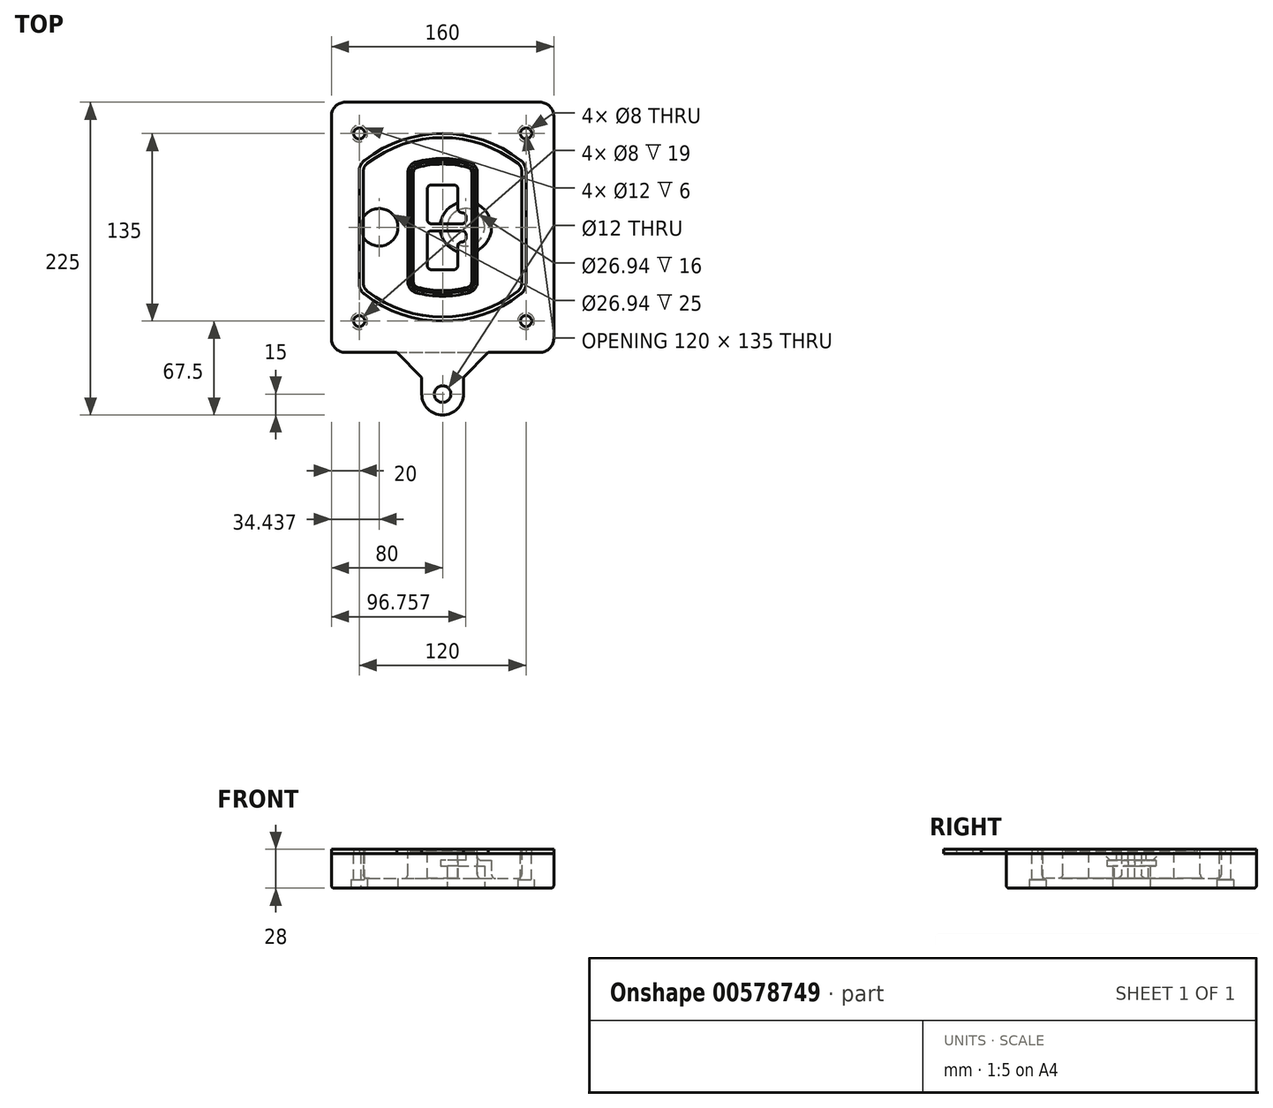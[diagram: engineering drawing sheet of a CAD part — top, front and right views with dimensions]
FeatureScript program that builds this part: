
annotation { "Feature Type Name" : "Feature", "Feature Type Description" : "" }
export const myFeature = defineFeature(function(context is Context, id is Id, definition is map)
    precondition{}
    {
        {
            var Q0;
            Q0=qCreatedBy(makeId("Top.planeOp"),FACE);
            var sketch = newSketch(context, id + "F0", { "sketchPlane" : qUnion([Q0])});
            skPoint(sketch, "E0.rect.middle", {"position": v(0, 0) * mm});
            skLineSegment(sketch, "E1.bottom", {"start": v(-70, -90) * mm, "end": v(70, -90) * mm});
            skLineSegment(sketch, "E1.top", {"start": v(-70, 90) * mm, "end": v(70, 90) * mm});
            skLineSegment(sketch, "E1.left", {"start": v(-80, -80) * mm, "end": v(-80, 80) * mm});
            skLineSegment(sketch, "E1.right", {"start": v(80, -80) * mm, "end": v(80, 80) * mm});
            skLineSegment(sketch, "E2", {"start": v(-80, 90) * mm, "end": v(80, -90) * mm, "construction": true});
            skLineSegment(sketch, "E3", {"start": v(80, 90) * mm, "end": v(-80, -90) * mm, "construction": true});
            skCircle(sketch, "E4", {"center": v(-60, 67.5) * mm, "radius": 4 * mm});
            skCircle(sketch, "E5", {"center": v(60, 67.5) * mm, "radius": 4 * mm});
            skCircle(sketch, "E6", {"center": v(60, -67.5) * mm, "radius": 4 * mm});
            skCircle(sketch, "E7", {"center": v(-60, -67.5) * mm, "radius": 4 * mm});
            skLineSegment(sketch, "E8", {"start": v(-60, 67.5) * mm, "end": v(60, 67.5) * mm, "construction": true});
            skLineSegment(sketch, "E9", {"start": v(60, 67.5) * mm, "end": v(60, -67.5) * mm, "construction": true});
            skLineSegment(sketch, "E10", {"start": v(60, -67.5) * mm, "end": v(-60, -67.5) * mm, "construction": true});
            skLineSegment(sketch, "E11", {"start": v(-60, -67.5) * mm, "end": v(-60, 67.5) * mm, "construction": true});
            skLineSegment(sketch, "E12", {"start": v(-60, 40.3) * mm, "end": v(-60, -40.3) * mm});
            skLineSegment(sketch, "E13", {"start": v(60, 40.3) * mm, "end": v(60, -40.3) * mm});
            skArc(sketch, "E14", {"start": v(56.15, 48.18) * mm, "mid": v(0, 67.5) * mm, "end": v(-56.15, 48.18) * mm});
            skArc(sketch, "E15", {"start": v(-56.15, -48.18) * mm, "mid": v(0, -67.5) * mm, "end": v(56.15, -48.18) * mm});
            skLineSegment(sketch, "E16", {"start": v(-60, 0) * mm, "end": v(60, 0) * mm, "construction": true});
            skPoint(sketch, "E17.visualSharp", {"position": v(-60, -45) * mm});
            skArc(sketch, "E17.filletArc", {"start": v(-60, -40.3) * mm, "mid": v(-58.99, -44.68) * mm, "end": v(-56.15, -48.18) * mm});
            skPoint(sketch, "E18.visualSharp", {"position": v(-60, 45) * mm});
            skArc(sketch, "E18.filletArc", {"start": v(-56.15, 48.18) * mm, "mid": v(-58.99, 44.68) * mm, "end": v(-60, 40.3) * mm});
            skPoint(sketch, "E19.visualSharp", {"position": v(60, 45) * mm});
            skArc(sketch, "E19.filletArc", {"start": v(60, 40.3) * mm, "mid": v(58.99, 44.68) * mm, "end": v(56.15, 48.18) * mm});
            skPoint(sketch, "E20.visualSharp", {"position": v(60, -45) * mm});
            skArc(sketch, "E20.filletArc", {"start": v(56.15, -48.18) * mm, "mid": v(58.99, -44.68) * mm, "end": v(60, -40.3) * mm});
            skPoint(sketch, "E21.visualSharp", {"position": v(-80, 90) * mm});
            skArc(sketch, "E21.filletArc", {"start": v(-70, 90) * mm, "mid": v(-77.07, 87.07) * mm, "end": v(-80, 80) * mm});
            skPoint(sketch, "E22.visualSharp", {"position": v(80, 90) * mm});
            skArc(sketch, "E22.filletArc", {"start": v(80, 80) * mm, "mid": v(77.07, 87.07) * mm, "end": v(70, 90) * mm});
            skPoint(sketch, "E23.visualSharp", {"position": v(80, -90) * mm});
            skArc(sketch, "E23.filletArc", {"start": v(70, -90) * mm, "mid": v(77.07, -87.07) * mm, "end": v(80, -80) * mm});
            skPoint(sketch, "E24.visualSharp", {"position": v(-80, -90) * mm});
            skArc(sketch, "E24.filletArc", {"start": v(-80, -80) * mm, "mid": v(-77.07, -87.07) * mm, "end": v(-70, -90) * mm});
            skArc(sketch, "E25.0", {"start": v(57, 40.3) * mm, "mid": v(56.3, 43.36) * mm, "end": v(54.3, 45.81) * mm});
            skLineSegment(sketch, "E25.1", {"start": v(57, 40.3) * mm, "end": v(57, -40.3) * mm});
            skArc(sketch, "E25.2", {"start": v(54.3, -45.81) * mm, "mid": v(56.3, -43.36) * mm, "end": v(57, -40.3) * mm});
            skArc(sketch, "E25.3", {"start": v(-54.3, -45.81) * mm, "mid": v(0, -64.5) * mm, "end": v(54.3, -45.81) * mm});
            skArc(sketch, "E25.4", {"start": v(-57, -40.3) * mm, "mid": v(-56.3, -43.36) * mm, "end": v(-54.3, -45.81) * mm});
            skArc(sketch, "E25.5", {"start": v(54.3, 45.81) * mm, "mid": v(0, 64.5) * mm, "end": v(-54.3, 45.81) * mm});
            skLineSegment(sketch, "E25.6", {"start": v(-57, 40.3) * mm, "end": v(-57, -40.3) * mm});
            skArc(sketch, "E25.7", {"start": v(-54.3, 45.81) * mm, "mid": v(-56.3, 43.36) * mm, "end": v(-57, 40.3) * mm});
            skArc(sketch, "E26.0", {"start": v(-58.62, 51.33) * mm, "mid": v(-62.58, 46.43) * mm, "end": v(-64, 40.3) * mm});
            skArc(sketch, "E26.1", {"start": v(58.62, 51.33) * mm, "mid": v(0, 71.5) * mm, "end": v(-58.62, 51.33) * mm});
            skArc(sketch, "E26.2", {"start": v(64, 40.3) * mm, "mid": v(62.58, 46.43) * mm, "end": v(58.62, 51.33) * mm});
            skLineSegment(sketch, "E26.3", {"start": v(64, 40.3) * mm, "end": v(64, -40.3) * mm});
            skArc(sketch, "E26.4", {"start": v(58.62, -51.33) * mm, "mid": v(62.58, -46.43) * mm, "end": v(64, -40.3) * mm});
            skLineSegment(sketch, "E26.5", {"start": v(-64, 40.3) * mm, "end": v(-64, -40.3) * mm});
            skArc(sketch, "E26.6", {"start": v(-58.62, -51.33) * mm, "mid": v(0, -71.5) * mm, "end": v(58.62, -51.33) * mm});
            skArc(sketch, "E26.7", {"start": v(-64, -40.3) * mm, "mid": v(-62.58, -46.43) * mm, "end": v(-58.62, -51.33) * mm});
            skSolve(sketch);
        }
        {
            var Q0;
            Q0=makeQuery(id+"F0.imprint","IMPRINT",FACE,{"disambiguationData":[TD([[makeQuery(id+"F0.imprint","IMPRINT",EDGE,{"derivedFrom":sQuery(id+"F0.wireOp",EDGE,"E1.bottom")}),1.0]])]});
            var Q1;
            Q1=makeQuery(id+"F0.imprint","IMPRINT",FACE,{"disambiguationData":[TD([[makeQuery(id+"F0.imprint","IMPRINT",EDGE,{"derivedFrom":sQuery(id+"F0.wireOp",EDGE,"E12")}),1.0]])]});
            var Q2;
            Q2=makeQuery(id+"F0.imprint","IMPRINT",FACE,{"disambiguationData":[TD([[makeQuery(id+"F0.imprint","IMPRINT",EDGE,{"derivedFrom":sQuery(id+"F0.wireOp",EDGE,"E25.0")}),1.0]])]});
            var Q3;
            Q3=makeQuery(id+"F0.imprint","IMPRINT",FACE,{"disambiguationData":[TD([[makeQuery(id+"F0.imprint","IMPRINT",EDGE,{"derivedFrom":sQuery(id+"F0.wireOp",EDGE,"E12")}),-1.0]])]});
            extrude(context, id + "F1", {"entities" : qUnion([Q0, Q1, Q2, Q3]), "oppositeDirection" : true, "depth" : 25 * mm});
        }
        {
            var Q0;
            Q0=makeQuery(id+"F0.imprint","IMPRINT",FACE,{"disambiguationData":[TD([[makeQuery(id+"F0.imprint","IMPRINT",EDGE,{"derivedFrom":sQuery(id+"F0.wireOp",EDGE,"E12")}),1.0]])]});
            extrude(context, id + "F2", {"entities" : qUnion([Q0]), "operationType" : NewBodyOperationType.ADD, "depth" : 3 * mm});
        }
        {
            var Q0;
            Q0=makeQuery(id+"F0.imprint","IMPRINT",FACE,{"disambiguationData":[TD([[makeQuery(id+"F0.imprint","IMPRINT",EDGE,{"derivedFrom":sQuery(id+"F0.wireOp",EDGE,"E25.0")}),1.0]])]});
            extrude(context, id + "F3", {"entities" : qUnion([Q0]), "operationType" : NewBodyOperationType.REMOVE, "oppositeDirection" : true, "depth" : 18 * mm});
        }
        {
            var Q0;
            Q0=makeQuery(id+"F2.opExtrude","CAP_FACE",FACE,{"disambiguationData":[OSD([sQuery(id+"F0.wireOp",EDGE,"E12"),sQuery(id+"F0.wireOp",EDGE,"E13"),sQuery(id+"F0.wireOp",EDGE,"E14"),sQuery(id+"F0.wireOp",EDGE,"E15"),sQuery(id+"F0.wireOp",EDGE,"E17.filletArc"),sQuery(id+"F0.wireOp",EDGE,"E18.filletArc"),sQuery(id+"F0.wireOp",EDGE,"E19.filletArc"),sQuery(id+"F0.wireOp",EDGE,"E20.filletArc"),sQuery(id+"F0.wireOp",EDGE,"E25.0"),sQuery(id+"F0.wireOp",EDGE,"E25.1"),sQuery(id+"F0.wireOp",EDGE,"E25.2"),sQuery(id+"F0.wireOp",EDGE,"E25.3"),sQuery(id+"F0.wireOp",EDGE,"E25.4"),sQuery(id+"F0.wireOp",EDGE,"E25.5"),sQuery(id+"F0.wireOp",EDGE,"E25.6"),sQuery(id+"F0.wireOp",EDGE,"E25.7")])],"isStart":false});
            var sketch = newSketch(context, id + "F4", { "sketchPlane" : qUnion([Q0])});
            skArc(sketch, "E27.0", {"start": v(-19.08, -46.97) * mm, "mid": v(0, -49.5) * mm, "end": v(19.08, -46.97) * mm});
            skArc(sketch, "E28.0", {"start": v(19.08, 46.97) * mm, "mid": v(0, 49.5) * mm, "end": v(-19.08, 46.97) * mm});
            skLineSegment(sketch, "E29", {"start": v(-25, 39.25) * mm, "end": v(-25, -39.25) * mm});
            skLineSegment(sketch, "E30", {"start": v(25, 39.25) * mm, "end": v(25, -39.25) * mm});
            skLineSegment(sketch, "E31", {"start": v(-25, 45.1) * mm, "end": v(25, 45.1) * mm, "construction": true});
            skLineSegment(sketch, "E32", {"start": v(-25, -45.1) * mm, "end": v(25, -45.1) * mm, "construction": true});
            skPoint(sketch, "E33.visualSharp", {"position": v(-25, 45.1) * mm});
            skArc(sketch, "E33.filletArc", {"start": v(-19.08, 46.97) * mm, "mid": v(-23.35, 44.11) * mm, "end": v(-25, 39.25) * mm});
            skPoint(sketch, "E34.visualSharp", {"position": v(25, 45.1) * mm});
            skArc(sketch, "E34.filletArc", {"start": v(25, 39.25) * mm, "mid": v(23.35, 44.11) * mm, "end": v(19.08, 46.97) * mm});
            skPoint(sketch, "E35.visualSharp", {"position": v(25, -45.1) * mm});
            skArc(sketch, "E35.filletArc", {"start": v(19.08, -46.97) * mm, "mid": v(23.35, -44.11) * mm, "end": v(25, -39.25) * mm});
            skPoint(sketch, "E36.visualSharp", {"position": v(-25, -45.1) * mm});
            skArc(sketch, "E36.filletArc", {"start": v(-25, -39.25) * mm, "mid": v(-23.35, -44.11) * mm, "end": v(-19.08, -46.97) * mm});
            skArc(sketch, "E37.0", {"start": v(54.3, 45.81) * mm, "mid": v(0, 64.5) * mm, "end": v(-54.3, 45.81) * mm});
            skArc(sketch, "E37.1", {"start": v(-54.3, 45.81) * mm, "mid": v(-56.3, 43.36) * mm, "end": v(-57, 40.3) * mm});
            skLineSegment(sketch, "E37.2", {"start": v(-57, 40.3) * mm, "end": v(-57, -40.3) * mm});
            skArc(sketch, "E37.3", {"start": v(-57, -40.3) * mm, "mid": v(-56.3, -43.36) * mm, "end": v(-54.3, -45.81) * mm});
            skArc(sketch, "E37.4", {"start": v(-54.3, -45.81) * mm, "mid": v(0, -64.5) * mm, "end": v(54.3, -45.81) * mm});
            skArc(sketch, "E37.5", {"start": v(54.3, -45.81) * mm, "mid": v(56.3, -43.36) * mm, "end": v(57, -40.3) * mm});
            skLineSegment(sketch, "E37.6", {"start": v(57, 40.3) * mm, "end": v(57, -40.3) * mm});
            skArc(sketch, "E37.7", {"start": v(57, 40.3) * mm, "mid": v(56.3, 43.36) * mm, "end": v(54.3, 45.81) * mm});
            skLineSegment(sketch, "E38.0", {"start": v(23, 39.25) * mm, "end": v(23, -39.25) * mm});
            skArc(sketch, "E38.1", {"start": v(18.56, -45.04) * mm, "mid": v(21.76, -42.9) * mm, "end": v(23, -39.25) * mm});
            skArc(sketch, "E38.2", {"start": v(-18.56, -45.04) * mm, "mid": v(0, -47.5) * mm, "end": v(18.56, -45.04) * mm});
            skArc(sketch, "E38.3", {"start": v(-23, -39.25) * mm, "mid": v(-21.76, -42.9) * mm, "end": v(-18.56, -45.04) * mm});
            skLineSegment(sketch, "E38.4", {"start": v(-23, 39.25) * mm, "end": v(-23, -39.25) * mm});
            skArc(sketch, "E38.5", {"start": v(23, 39.25) * mm, "mid": v(21.76, 42.9) * mm, "end": v(18.56, 45.04) * mm});
            skArc(sketch, "E38.6", {"start": v(-18.56, 45.04) * mm, "mid": v(-21.76, 42.9) * mm, "end": v(-23, 39.25) * mm});
            skArc(sketch, "E38.7", {"start": v(18.56, 45.04) * mm, "mid": v(0, 47.5) * mm, "end": v(-18.56, 45.04) * mm});
            skArc(sketch, "E39.0", {"start": v(21, 39.25) * mm, "mid": v(20.18, 41.68) * mm, "end": v(18.04, 43.1) * mm});
            skLineSegment(sketch, "E39.1", {"start": v(21, 39.25) * mm, "end": v(21, -39.25) * mm});
            skArc(sketch, "E39.2", {"start": v(18.04, -43.1) * mm, "mid": v(20.18, -41.68) * mm, "end": v(21, -39.25) * mm});
            skArc(sketch, "E39.3", {"start": v(-18.04, -43.1) * mm, "mid": v(0, -45.5) * mm, "end": v(18.04, -43.1) * mm});
            skArc(sketch, "E39.4", {"start": v(-21, -39.25) * mm, "mid": v(-20.18, -41.68) * mm, "end": v(-18.04, -43.1) * mm});
            skArc(sketch, "E39.5", {"start": v(18.04, 43.1) * mm, "mid": v(0, 45.5) * mm, "end": v(-18.04, 43.1) * mm});
            skLineSegment(sketch, "E39.6", {"start": v(-21, 39.25) * mm, "end": v(-21, -39.25) * mm});
            skArc(sketch, "E39.7", {"start": v(-18.04, 43.1) * mm, "mid": v(-20.18, 41.68) * mm, "end": v(-21, 39.25) * mm});
            skLineSegment(sketch, "E40", {"start": v(-25, 0) * mm, "end": v(25, 0) * mm, "construction": true});
            skLineSegment(sketch, "E41", {"start": v(-11, 5.5) * mm, "end": v(-11, 27.5) * mm});
            skLineSegment(sketch, "E42", {"start": v(-8, 30.5) * mm, "end": v(8, 30.5) * mm});
            skLineSegment(sketch, "E43", {"start": v(11, 27.5) * mm, "end": v(11, 13.5) * mm});
            skLineSegment(sketch, "E44", {"start": v(14, 10.5) * mm, "end": v(14, 10.5) * mm});
            skLineSegment(sketch, "E45", {"start": v(17, 7.5) * mm, "end": v(17, 5.5) * mm});
            skLineSegment(sketch, "E46", {"start": v(14, 2.5) * mm, "end": v(-8, 2.5) * mm});
            skPoint(sketch, "E47.visualSharp", {"position": v(-11, 30.5) * mm});
            skArc(sketch, "E47.filletArc", {"start": v(-8, 30.5) * mm, "mid": v(-10.12, 29.62) * mm, "end": v(-11, 27.5) * mm});
            skPoint(sketch, "E48.visualSharp", {"position": v(11, 30.5) * mm});
            skArc(sketch, "E48.filletArc", {"start": v(11, 27.5) * mm, "mid": v(10.12, 29.62) * mm, "end": v(8, 30.5) * mm});
            skPoint(sketch, "E49.visualSharp", {"position": v(11, 10.5) * mm});
            skArc(sketch, "E49.filletArc", {"start": v(11, 13.5) * mm, "mid": v(11.88, 11.38) * mm, "end": v(14, 10.5) * mm});
            skPoint(sketch, "E50.visualSharp", {"position": v(17, 10.5) * mm});
            skArc(sketch, "E50.filletArc", {"start": v(17, 7.5) * mm, "mid": v(16.12, 9.62) * mm, "end": v(14, 10.5) * mm});
            skPoint(sketch, "E51.visualSharp", {"position": v(17, 2.5) * mm});
            skArc(sketch, "E51.filletArc", {"start": v(14, 2.5) * mm, "mid": v(16.12, 3.38) * mm, "end": v(17, 5.5) * mm});
            skPoint(sketch, "E52.visualSharp", {"position": v(-11, 2.5) * mm});
            skArc(sketch, "E52.filletArc", {"start": v(-11, 5.5) * mm, "mid": v(-10.12, 3.38) * mm, "end": v(-8, 2.5) * mm});
            skLineSegment(sketch, "E53.0.MirrorCS", {"start": v(14, -2.5) * mm, "end": v(-8, -2.5) * mm});
            skArc(sketch, "E54.0.MirrorCS", {"start": v(-11, -5.5) * mm, "mid": v(-10.12, -3.38) * mm, "end": v(-8, -2.5) * mm});
            skLineSegment(sketch, "E55.0.MirrorCS", {"start": v(-11, -5.5) * mm, "end": v(-11, -27.5) * mm});
            skArc(sketch, "E56.0.MirrorCS", {"start": v(-8, -30.5) * mm, "mid": v(-10.12, -29.62) * mm, "end": v(-11, -27.5) * mm});
            skLineSegment(sketch, "E57.0.MirrorCS", {"start": v(-8, -30.5) * mm, "end": v(8, -30.5) * mm});
            skArc(sketch, "E58.0.MirrorCS", {"start": v(11, -27.5) * mm, "mid": v(10.12, -29.62) * mm, "end": v(8, -30.5) * mm});
            skLineSegment(sketch, "E59.0.MirrorCS", {"start": v(11, -27.5) * mm, "end": v(11, -13.5) * mm});
            skArc(sketch, "E60.0.MirrorCS", {"start": v(11, -13.5) * mm, "mid": v(11.88, -11.38) * mm, "end": v(14, -10.5) * mm});
            skArc(sketch, "E61.0.MirrorCS", {"start": v(17, -7.5) * mm, "mid": v(16.12, -9.62) * mm, "end": v(14, -10.5) * mm});
            skLineSegment(sketch, "E62.0.MirrorCS", {"start": v(17, -7.5) * mm, "end": v(17, -5.5) * mm});
            skArc(sketch, "E63.0.MirrorCS", {"start": v(14, -2.5) * mm, "mid": v(16.12, -3.38) * mm, "end": v(17, -5.5) * mm});
            skSolve(sketch);
        }
        {
            var Q0;
            Q0=makeQuery(id+"F4.imprint","IMPRINT",FACE,{"disambiguationData":[TD([[makeQuery(id+"F4.imprint","IMPRINT",EDGE,{"derivedFrom":sQuery(id+"F4.wireOp",EDGE,"E27.0")}),1.0]])]});
            var Q1;
            Q1=makeQuery(id+"F4.imprint","IMPRINT",FACE,{"disambiguationData":[TD([[makeQuery(id+"F4.imprint","IMPRINT",EDGE,{"derivedFrom":sQuery(id+"F4.wireOp",EDGE,"E38.0")}),-1.0]])]});
            var Q2;
            Q2=makeQuery(id+"F4.imprint","IMPRINT",FACE,{"disambiguationData":[TD([[makeQuery(id+"F4.imprint","IMPRINT",EDGE,{"derivedFrom":sQuery(id+"F4.wireOp",EDGE,"E39.0")}),1.0]])]});
            extrude(context, id + "F5", {"entities" : qUnion([Q0, Q1, Q2]), "operationType" : NewBodyOperationType.ADD, "endBound" : BoundingType.UP_TO_NEXT, "oppositeDirection" : true, "depth" : 25 * mm});
        }
        {
            var Q0;
            Q0=makeQuery(id+"F4.imprint","IMPRINT",FACE,{"disambiguationData":[TD([[makeQuery(id+"F4.imprint","IMPRINT",EDGE,{"derivedFrom":sQuery(id+"F4.wireOp",EDGE,"E38.0")}),-1.0]])]});
            extrude(context, id + "F6", {"entities" : qUnion([Q0]), "operationType" : NewBodyOperationType.REMOVE, "oppositeDirection" : true, "depth" : 2 * mm});
        }
        {
            var Q0;
            Q0=makeQuery(id+"F1.opExtrude","CAP_FACE",FACE,{"disambiguationData":[OSD([sQuery(id+"F0.wireOp",EDGE,"E1.bottom"),sQuery(id+"F0.wireOp",EDGE,"E1.top"),sQuery(id+"F0.wireOp",EDGE,"E1.left"),sQuery(id+"F0.wireOp",EDGE,"E1.right"),sQuery(id+"F0.wireOp",EDGE,"E4"),sQuery(id+"F0.wireOp",EDGE,"E5"),sQuery(id+"F0.wireOp",EDGE,"E6"),sQuery(id+"F0.wireOp",EDGE,"E7"),sQuery(id+"F0.wireOp",EDGE,"E21.filletArc"),sQuery(id+"F0.wireOp",EDGE,"E22.filletArc"),sQuery(id+"F0.wireOp",EDGE,"E23.filletArc"),sQuery(id+"F0.wireOp",EDGE,"E24.filletArc")])],"isStart":false});
            var sketch = newSketch(context, id + "F7", { "sketchPlane" : qUnion([Q0])});
            skCircle(sketch, "E64", {"center": v(16.76, 0) * mm, "radius": 13.47 * mm});
            skCircle(sketch, "E65", {"center": v(-45.56, 0) * mm, "radius": 13.47 * mm});
            skLineSegment(sketch, "E66", {"start": v(80, 0) * mm, "end": v(-80, 0) * mm});
            skCircle(sketch, "E67", {"center": v(16.76, 0) * mm, "radius": 18.47 * mm});
            skCircle(sketch, "E68", {"center": v(60, -67.5) * mm, "radius": 6 * mm});
            skCircle(sketch, "E69", {"center": v(-60, -67.5) * mm, "radius": 6 * mm});
            skCircle(sketch, "E70", {"center": v(-60, 67.5) * mm, "radius": 6 * mm});
            skCircle(sketch, "E71", {"center": v(60, 67.5) * mm, "radius": 6 * mm});
            skSolve(sketch);
        }
        {
            var Q0;
            {var subQ1=sQuery(id+"F7.wireOp",EDGE,"E66");var subQ4=sQuery(id+"F7.wireOp",EDGE,"E64");var subQ6=makeQuery(id+"F7.imprint","INTERSECT",VERTEX,{"disambiguationData":[OD(0.0)],"derivedFrom":[subQ4,subQ1]});Q0=makeQuery(id+"F7.imprint","IMPRINT",FACE,{"disambiguationData":[TD([[makeQuery(id+"F7.imprint","IMPRINT",EDGE,{"disambiguationData":[TD([[subQ6,-1.0]])],"derivedFrom":subQ4}),-1.0]])]});}
            var Q1;
            {var subQ0=sQuery(id+"F7.wireOp",EDGE,"E66");var subQ1=sQuery(id+"F7.wireOp",EDGE,"E64");var subQ3=makeQuery(id+"F7.imprint","INTERSECT",VERTEX,{"disambiguationData":[OD(0.0)],"derivedFrom":[subQ1,subQ0]});Q1=makeQuery(id+"F7.imprint","IMPRINT",FACE,{"disambiguationData":[TD([[makeQuery(id+"F7.imprint","IMPRINT",EDGE,{"disambiguationData":[TD([[subQ3,-1.0]])],"derivedFrom":subQ1}),1.0]])]});}
            var Q2;
            {var subQ0=sQuery(id+"F7.wireOp",EDGE,"E66");var subQ1=sQuery(id+"F7.wireOp",EDGE,"E64");var subQ3=makeQuery(id+"F7.imprint","INTERSECT",VERTEX,{"disambiguationData":[OD(0.0)],"derivedFrom":[subQ1,subQ0]});Q2=makeQuery(id+"F7.imprint","IMPRINT",FACE,{"disambiguationData":[TD([[makeQuery(id+"F7.imprint","IMPRINT",EDGE,{"disambiguationData":[TD([[subQ3,1.0]])],"derivedFrom":subQ1}),1.0]])]});}
            var Q3;
            {var subQ1=sQuery(id+"F7.wireOp",EDGE,"E66");var subQ4=sQuery(id+"F7.wireOp",EDGE,"E64");var subQ6=makeQuery(id+"F7.imprint","INTERSECT",VERTEX,{"disambiguationData":[OD(0.0)],"derivedFrom":[subQ4,subQ1]});Q3=makeQuery(id+"F7.imprint","IMPRINT",FACE,{"disambiguationData":[TD([[makeQuery(id+"F7.imprint","IMPRINT",EDGE,{"disambiguationData":[TD([[subQ6,1.0]])],"derivedFrom":subQ4}),-1.0]])]});}
            extrude(context, id + "F8", {"entities" : qUnion([Q0, Q1, Q2, Q3]), "operationType" : NewBodyOperationType.ADD, "oppositeDirection" : true, "depth" : 20 * mm});
        }
        {
            var Q0;
            {var subQ0=sQuery(id+"F7.wireOp",EDGE,"E66");var subQ1=sQuery(id+"F7.wireOp",EDGE,"E64");var subQ3=makeQuery(id+"F7.imprint","INTERSECT",VERTEX,{"disambiguationData":[OD(0.0)],"derivedFrom":[subQ1,subQ0]});Q0=makeQuery(id+"F7.imprint","IMPRINT",FACE,{"disambiguationData":[TD([[makeQuery(id+"F7.imprint","IMPRINT",EDGE,{"disambiguationData":[TD([[subQ3,-1.0]])],"derivedFrom":subQ1}),1.0]])]});}
            var Q1;
            {var subQ0=sQuery(id+"F7.wireOp",EDGE,"E66");var subQ1=sQuery(id+"F7.wireOp",EDGE,"E64");var subQ3=makeQuery(id+"F7.imprint","INTERSECT",VERTEX,{"disambiguationData":[OD(0.0)],"derivedFrom":[subQ1,subQ0]});Q1=makeQuery(id+"F7.imprint","IMPRINT",FACE,{"disambiguationData":[TD([[makeQuery(id+"F7.imprint","IMPRINT",EDGE,{"disambiguationData":[TD([[subQ3,1.0]])],"derivedFrom":subQ1}),1.0]])]});}
            extrude(context, id + "F9", {"entities" : qUnion([Q0, Q1]), "operationType" : NewBodyOperationType.REMOVE, "oppositeDirection" : true, "depth" : 16 * mm});
        }
        {
            var Q0;
            {var subQ0=sQuery(id+"F7.wireOp",EDGE,"E66");var subQ1=sQuery(id+"F7.wireOp",EDGE,"E65");var subQ3=makeQuery(id+"F7.imprint","INTERSECT",VERTEX,{"disambiguationData":[OD(0.0)],"derivedFrom":[subQ1,subQ0]});Q0=makeQuery(id+"F7.imprint","IMPRINT",FACE,{"disambiguationData":[TD([[makeQuery(id+"F7.imprint","IMPRINT",EDGE,{"disambiguationData":[TD([[subQ3,-1.0]])],"derivedFrom":subQ1}),1.0]])]});}
            var Q1;
            {var subQ0=sQuery(id+"F7.wireOp",EDGE,"E66");var subQ1=sQuery(id+"F7.wireOp",EDGE,"E65");var subQ3=makeQuery(id+"F7.imprint","INTERSECT",VERTEX,{"disambiguationData":[OD(0.0)],"derivedFrom":[subQ1,subQ0]});Q1=makeQuery(id+"F7.imprint","IMPRINT",FACE,{"disambiguationData":[TD([[makeQuery(id+"F7.imprint","IMPRINT",EDGE,{"disambiguationData":[TD([[subQ3,1.0]])],"derivedFrom":subQ1}),1.0]])]});}
            extrude(context, id + "F10", {"entities" : qUnion([Q0, Q1]), "operationType" : NewBodyOperationType.REMOVE, "oppositeDirection" : true, "depth" : 25 * mm});
        }
        {
            var Q0;
            Q0=makeQuery(id+"F7.imprint","IMPRINT",FACE,{"disambiguationData":[TD([[makeQuery(id+"F7.imprint","IMPRINT",EDGE,{"derivedFrom":sQuery(id+"F7.wireOp",EDGE,"E68")}),1.0]])]});
            var Q1;
            Q1=makeQuery(id+"F7.imprint","IMPRINT",FACE,{"disambiguationData":[TD([[makeQuery(id+"F7.imprint","IMPRINT",EDGE,{"derivedFrom":makeQuery(id+"F1.opExtrude","CAP_EDGE",EDGE,{"disambiguationData":[OSD([sQuery(id+"F0.wireOp",EDGE,"E5")])],"isStart":false})}),-1.0]])]});
            var Q2;
            Q2=makeQuery(id+"F7.imprint","IMPRINT",FACE,{"disambiguationData":[TD([[makeQuery(id+"F7.imprint","IMPRINT",EDGE,{"derivedFrom":sQuery(id+"F7.wireOp",EDGE,"E69")}),1.0]])]});
            var Q3;
            Q3=makeQuery(id+"F7.imprint","IMPRINT",FACE,{"disambiguationData":[TD([[makeQuery(id+"F7.imprint","IMPRINT",EDGE,{"derivedFrom":makeQuery(id+"F1.opExtrude","CAP_EDGE",EDGE,{"disambiguationData":[OSD([sQuery(id+"F0.wireOp",EDGE,"E4")])],"isStart":false})}),-1.0]])]});
            var Q4;
            Q4=makeQuery(id+"F7.imprint","IMPRINT",FACE,{"disambiguationData":[TD([[makeQuery(id+"F7.imprint","IMPRINT",EDGE,{"derivedFrom":sQuery(id+"F7.wireOp",EDGE,"E70")}),1.0]])]});
            var Q5;
            Q5=makeQuery(id+"F7.imprint","IMPRINT",FACE,{"disambiguationData":[TD([[makeQuery(id+"F7.imprint","IMPRINT",EDGE,{"derivedFrom":makeQuery(id+"F1.opExtrude","CAP_EDGE",EDGE,{"disambiguationData":[OSD([sQuery(id+"F0.wireOp",EDGE,"E7")])],"isStart":false})}),-1.0]])]});
            var Q6;
            Q6=makeQuery(id+"F7.imprint","IMPRINT",FACE,{"disambiguationData":[TD([[makeQuery(id+"F7.imprint","IMPRINT",EDGE,{"derivedFrom":sQuery(id+"F7.wireOp",EDGE,"E71")}),1.0]])]});
            var Q7;
            Q7=makeQuery(id+"F7.imprint","IMPRINT",FACE,{"disambiguationData":[TD([[makeQuery(id+"F7.imprint","IMPRINT",EDGE,{"derivedFrom":makeQuery(id+"F1.opExtrude","CAP_EDGE",EDGE,{"disambiguationData":[OSD([sQuery(id+"F0.wireOp",EDGE,"E6")])],"isStart":false})}),-1.0]])]});
            extrude(context, id + "F11", {"entities" : qUnion([Q0, Q1, Q2, Q3, Q4, Q5, Q6, Q7]), "operationType" : NewBodyOperationType.REMOVE, "oppositeDirection" : true, "depth" : 6 * mm});
        }
        {
            var Q0;
            Q0=makeQuery(id+"F9.boolean.opBoolean","COPY",FACE,{"derivedFrom":makeQuery(id+"F9.opExtrude","CAP_FACE",FACE,{"disambiguationData":[OSD([sQuery(id+"F7.wireOp",EDGE,"E64")])],"isStart":false})});
            var sketch = newSketch(context, id + "F12", { "sketchPlane" : qUnion([Q0])});
            skArc(sketch, "E72.0", {"start": v(11, 17.55) * mm, "mid": v(2.57, 11.82) * mm, "end": v(-1.54, 2.5) * mm});
            skArc(sketch, "E72.1", {"start": v(-1.54, -2.5) * mm, "mid": v(2.57, -11.82) * mm, "end": v(11, -17.55) * mm});
            skLineSegment(sketch, "E73", {"start": v(-1.54, -2.5) * mm, "end": v(14, -2.5) * mm});
            skLineSegment(sketch, "E74.0", {"start": v(14, 2.5) * mm, "end": v(-1.54, 2.5) * mm});
            skArc(sketch, "E74.1", {"start": v(14, 2.5) * mm, "mid": v(16.12, 3.38) * mm, "end": v(17, 5.5) * mm});
            skLineSegment(sketch, "E74.2", {"start": v(17, 7.5) * mm, "end": v(17, 5.5) * mm});
            skArc(sketch, "E74.3", {"start": v(17, 7.5) * mm, "mid": v(16.12, 9.62) * mm, "end": v(14, 10.5) * mm});
            skArc(sketch, "E74.4", {"start": v(11, 13.5) * mm, "mid": v(11.88, 11.38) * mm, "end": v(14, 10.5) * mm});
            skLineSegment(sketch, "E74.5", {"start": v(11, 17.55) * mm, "end": v(11, 13.5) * mm});
            skLineSegment(sketch, "E74.7", {"start": v(14, -2.5) * mm, "end": v(-1.54, -2.5) * mm});
            skArc(sketch, "E74.8", {"start": v(14, -2.5) * mm, "mid": v(16.12, -3.38) * mm, "end": v(17, -5.5) * mm});
            skLineSegment(sketch, "E74.9", {"start": v(17, -7.5) * mm, "end": v(17, -5.5) * mm});
            skArc(sketch, "E74.10", {"start": v(17, -7.5) * mm, "mid": v(16.12, -9.62) * mm, "end": v(14, -10.5) * mm});
            skArc(sketch, "E74.11", {"start": v(11, -13.5) * mm, "mid": v(11.88, -11.38) * mm, "end": v(14, -10.5) * mm});
            skLineSegment(sketch, "E74.12", {"start": v(11, -17.55) * mm, "end": v(11, -13.5) * mm});
            skPoint(sketch, "E75.orphan", {"position": v(11, -27.5) * mm});
            skPoint(sketch, "E76.orphan", {"position": v(-8, -2.5) * mm});
            skPoint(sketch, "E77.orphan", {"position": v(-8, 2.5) * mm});
            skPoint(sketch, "E78.orphan", {"position": v(11, 27.5) * mm});
            skSolve(sketch);
        }
        {
            var Q0;
            {var subQ7=sQuery(id+"F12.wireOp",EDGE,"E72.0");var subQ14=sQuery(id+"F12.wireOp",EDGE,"E72.1");var subQ16=sQuery(id+"F12.wireOp",EDGE,"E74.1");var subQ18=sQuery(id+"F12.wireOp",EDGE,"E74.8");Q0=qUnion([makeQuery(id+"F12.imprint","IMPRINT",FACE,{"disambiguationData":[TD([[makeQuery(id+"F12.imprint","IMPRINT",EDGE,{"derivedFrom":subQ7}),1.0]])]}),makeQuery(id+"F12.imprint","IMPRINT",FACE,{"disambiguationData":[TD([[makeQuery(id+"F12.imprint","IMPRINT",EDGE,{"derivedFrom":subQ14}),1.0]])]}),makeQuery(id+"F12.imprint","IMPRINT",FACE,{"disambiguationData":[TD([[makeQuery(id+"F12.imprint","IMPRINT",EDGE,{"derivedFrom":subQ16}),1.0]])]}),makeQuery(id+"F12.imprint","IMPRINT",FACE,{"disambiguationData":[TD([[makeQuery(id+"F12.imprint","IMPRINT",EDGE,{"derivedFrom":subQ18}),-1.0]])]})]);}
            var Q1;
            Q1=makeQuery(id+"F5.boolean.opBoolean","SPLIT",FACE,{"disambiguationData":[TD([makeQuery(id+"F5.opExtrude","SWEPT_FACE",FACE,{"disambiguationData":[OSD([sQuery(id+"F4.wireOp",EDGE,"E41")])]})])],"derivedFrom":makeQuery(id+"F3.boolean.opBoolean","COPY",FACE,{"derivedFrom":makeQuery(id+"F3.opExtrude","CAP_FACE",FACE,{"disambiguationData":[OSD([sQuery(id+"F0.wireOp",EDGE,"E25.0"),sQuery(id+"F0.wireOp",EDGE,"E25.1"),sQuery(id+"F0.wireOp",EDGE,"E25.2"),sQuery(id+"F0.wireOp",EDGE,"E25.3"),sQuery(id+"F0.wireOp",EDGE,"E25.4"),sQuery(id+"F0.wireOp",EDGE,"E25.5"),sQuery(id+"F0.wireOp",EDGE,"E25.6"),sQuery(id+"F0.wireOp",EDGE,"E25.7")])],"isStart":false})})});
            extrude(context, id + "F13", {"entities" : qUnion([Q0]), "operationType" : NewBodyOperationType.REMOVE, "endBound" : BoundingType.UP_TO_SURFACE, "endBoundEntityFace" : qUnion([Q1]), "depth" : 25 * mm});
        }
        {
            var Q0;
            Q0=makeQuery(id+"F3.boolean.opBoolean","COPY",EDGE,{"derivedFrom":makeQuery(id+"F3.opExtrude","CAP_EDGE",EDGE,{"disambiguationData":[OSD([sQuery(id+"F0.wireOp",EDGE,"E25.6")])],"isStart":false})});
            var Q1;
            Q1=makeQuery(id+"F8.boolean.opBoolean","INTERSECT",EDGE,{"derivedFrom":[makeQuery(id+"F5.opExtrude","SWEPT_FACE",FACE,{"disambiguationData":[OSD([sQuery(id+"F4.wireOp",EDGE,"E30")])]}),makeQuery(id+"F8.opExtrude","CAP_FACE",FACE,{"disambiguationData":[OSD([sQuery(id+"F7.wireOp",EDGE,"E67")])],"isStart":false})]});
            var Q2;
            Q2=makeQuery(id+"F8.boolean.opBoolean","INTERSECT",EDGE,{"disambiguationData":[OD(1.0)],"derivedFrom":[makeQuery(id+"F5.opExtrude","SWEPT_FACE",FACE,{"disambiguationData":[OSD([sQuery(id+"F4.wireOp",EDGE,"E30")])]}),makeQuery(id+"F8.opExtrude","SWEPT_FACE",FACE,{"disambiguationData":[OSD([sQuery(id+"F7.wireOp",EDGE,"E67")])]})]});
            var Q3;
            {var subQ0=sQuery(id+"F4.wireOp",EDGE,"E30");Q3=makeQuery(id+"F8.boolean.opBoolean","SPLIT",EDGE,{"disambiguationData":[TD([makeQuery(id+"F5.opExtrude","SWEPT_FACE",FACE,{"disambiguationData":[OSD([sQuery(id+"F4.wireOp",EDGE,"E35.filletArc")])]})])],"derivedFrom":makeQuery(id+"F5.opExtrude","CAP_EDGE",EDGE,{"disambiguationData":[OSD([subQ0])],"isStart":false})});}
            var Q4;
            {var subQ0=sQuery(id+"F0.wireOp",EDGE,"E25.7");var subQ1=sQuery(id+"F0.wireOp",EDGE,"E25.1");var subQ2=sQuery(id+"F0.wireOp",EDGE,"E25.6");var subQ3=sQuery(id+"F0.wireOp",EDGE,"E25.5");var subQ4=sQuery(id+"F0.wireOp",EDGE,"E25.4");var subQ5=sQuery(id+"F0.wireOp",EDGE,"E25.0");var subQ6=sQuery(id+"F0.wireOp",EDGE,"E25.2");var subQ7=sQuery(id+"F0.wireOp",EDGE,"E25.3");Q4=makeQuery(id+"F8.boolean.opBoolean","INTERSECT",EDGE,{"derivedFrom":[makeQuery(id+"F5.boolean.opBoolean","SPLIT",FACE,{"disambiguationData":[TD([makeQuery(id+"F2.opExtrude","SWEPT_FACE",FACE,{"disambiguationData":[OSD([subQ5])]})])],"derivedFrom":makeQuery(id+"F3.boolean.opBoolean","COPY",FACE,{"derivedFrom":makeQuery(id+"F3.opExtrude","CAP_FACE",FACE,{"disambiguationData":[OSD([subQ5,subQ1,subQ6,subQ7,subQ4,subQ3,subQ2,subQ0])],"isStart":false})})}),makeQuery(id+"F8.opExtrude","SWEPT_FACE",FACE,{"disambiguationData":[OSD([sQuery(id+"F7.wireOp",EDGE,"E67")])]})]});}
            var Q5;
            Q5=makeQuery(id+"F8.boolean.opBoolean","INTERSECT",EDGE,{"disambiguationData":[OD(0.0)],"derivedFrom":[makeQuery(id+"F5.opExtrude","SWEPT_FACE",FACE,{"disambiguationData":[OSD([sQuery(id+"F4.wireOp",EDGE,"E30")])]}),makeQuery(id+"F8.opExtrude","SWEPT_FACE",FACE,{"disambiguationData":[OSD([sQuery(id+"F7.wireOp",EDGE,"E67")])]})]});
            fillet(context, id + "F14", {"entities" : qUnion([Q0, Q1, Q2, Q3, Q4, Q5]), "radius" : 3 * mm, "tangentPropagation" : true, "allowEdgeOverflow" : false});
        }
        {
            var Q0;
            Q0=makeQuery(id+"F1.opExtrude","CAP_EDGE",EDGE,{"disambiguationData":[OSD([sQuery(id+"F0.wireOp",EDGE,"E1.bottom")])],"isStart":false});
            fillet(context, id + "F15", {"entities" : qUnion([Q0]), "radius" : 2 * mm, "tangentPropagation" : true, "allowEdgeOverflow" : false});
        }
        {
            var Q0;
            {var subQ0=sQuery(id+"F0.wireOp",EDGE,"E21.filletArc");var subQ1=sQuery(id+"F0.wireOp",EDGE,"E7");var subQ2=sQuery(id+"F0.wireOp",EDGE,"E6");var subQ3=sQuery(id+"F0.wireOp",EDGE,"E5");var subQ4=sQuery(id+"F0.wireOp",EDGE,"E4");var subQ5=sQuery(id+"F0.wireOp",EDGE,"E22.filletArc");var subQ6=sQuery(id+"F0.wireOp",EDGE,"E1.bottom");var subQ7=sQuery(id+"F0.wireOp",EDGE,"E1.right");var subQ8=sQuery(id+"F0.wireOp",EDGE,"E1.top");var subQ9=sQuery(id+"F0.wireOp",EDGE,"E1.left");var subQ10=sQuery(id+"F0.wireOp",EDGE,"E23.filletArc");var subQ11=sQuery(id+"F0.wireOp",EDGE,"E24.filletArc");Q0=makeQuery(id+"F2.boolean.opBoolean","SPLIT",FACE,{"disambiguationData":[TD([makeQuery(id+"F1.opExtrude","SWEPT_FACE",FACE,{"disambiguationData":[OSD([subQ6])]})])],"derivedFrom":makeQuery(id+"F1.opExtrude","CAP_FACE",FACE,{"disambiguationData":[OSD([subQ6,subQ8,subQ9,subQ7,subQ4,subQ3,subQ2,subQ1,subQ0,subQ5,subQ10,subQ11])],"isStart":true})});}
            var sketch = newSketch(context, id + "F16", { "sketchPlane" : qUnion([Q0])});
            skLineSegment(sketch, "E79", {"start": v(0, 90) * mm, "end": v(0, 120) * mm, "construction": true});
            skCircle(sketch, "E80", {"center": v(0, 120) * mm, "radius": 6 * mm});
            skLineSegment(sketch, "E81", {"start": v(-15, 108) * mm, "end": v(-33, 90) * mm});
            skLineSegment(sketch, "E82", {"start": v(-15, 120) * mm, "end": v(-15, 108) * mm});
            skLineSegment(sketch, "E83", {"start": v(15, 108) * mm, "end": v(33, 90) * mm});
            skLineSegment(sketch, "E84", {"start": v(15, 108) * mm, "end": v(15, 120) * mm});
            skArc(sketch, "E85", {"start": v(15, 120) * mm, "mid": v(0, 135) * mm, "end": v(-15, 120) * mm});
            skPoint(sketch, "E86.endSnap0", {"position": v(80, 0) * mm});
            skLineSegment(sketch, "E87.MirrorCS", {"start": v(-15, 108) * mm, "end": v(-15, 120) * mm});
            skArc(sketch, "E88.MirrorCS", {"start": v(-15, 120) * mm, "mid": v(0, 135) * mm, "end": v(15, 120) * mm});
            skLineSegment(sketch, "E89.MirrorCS", {"start": v(15, 120) * mm, "end": v(15, 108) * mm});
            skLineSegment(sketch, "E90", {"start": v(-104.02, 0) * mm, "end": v(105.57, 0) * mm, "construction": true});
            skPoint(sketch, "E90.endSnap0", {"position": v(60, 0) * mm});
            skLineSegment(sketch, "E91.MirrorCS", {"start": v(-15, -108) * mm, "end": v(-33, -90) * mm});
            skLineSegment(sketch, "E92.MirrorCS", {"start": v(15, -108) * mm, "end": v(33, -90) * mm});
            skLineSegment(sketch, "E93.MirrorCS", {"start": v(-15, -108) * mm, "end": v(-15, -120) * mm});
            skLineSegment(sketch, "E94.MirrorCS", {"start": v(15, -120) * mm, "end": v(15, -108) * mm});
            skLineSegment(sketch, "E95.MirrorCS", {"start": v(0, -90) * mm, "end": v(0, -120) * mm, "construction": true});
            skCircle(sketch, "E96.MirrorC", {"center": v(0, -120) * mm, "radius": 6 * mm});
            skArc(sketch, "E97.MirrorCS", {"start": v(-15, -120) * mm, "mid": v(0, -135) * mm, "end": v(15, -120) * mm});
            skSolve(sketch);
        }
        {
            var Q0;
            Q0=makeQuery(id+"F16.imprint","IMPRINT",FACE,{"disambiguationData":[TD([[makeQuery(id+"F16.imprint","IMPRINT",EDGE,{"derivedFrom":sQuery(id+"F16.wireOp",EDGE,"E87.MirrorCS")}),-1.0]])]});
            var Q1;
            Q1=makeQuery(id+"F16.imprint","IMPRINT",FACE,{"disambiguationData":[TD([[makeQuery(id+"F16.imprint","IMPRINT",EDGE,{"derivedFrom":makeQuery(id+"F1.opExtrude","CAP_EDGE",EDGE,{"disambiguationData":[OSD([sQuery(id+"F0.wireOp",EDGE,"E1.left")])],"isStart":true})}),-1.0]])]});
            var Q2;
            {var subQ1=sQuery(id+"F16.wireOp",EDGE,"E91.MirrorCS");Q2=makeQuery(id+"F16.imprint","IMPRINT",FACE,{"disambiguationData":[TD([[makeQuery(id+"F16.imprint","IMPRINT",EDGE,{"derivedFrom":subQ1}),-1.0]])]});}
            var Q3;
            Q3=makeQuery(id+"F2.opExtrude","CAP_FACE",FACE,{"disambiguationData":[OSD([sQuery(id+"F0.wireOp",EDGE,"E12"),sQuery(id+"F0.wireOp",EDGE,"E13"),sQuery(id+"F0.wireOp",EDGE,"E14"),sQuery(id+"F0.wireOp",EDGE,"E15"),sQuery(id+"F0.wireOp",EDGE,"E17.filletArc"),sQuery(id+"F0.wireOp",EDGE,"E18.filletArc"),sQuery(id+"F0.wireOp",EDGE,"E19.filletArc"),sQuery(id+"F0.wireOp",EDGE,"E20.filletArc"),sQuery(id+"F0.wireOp",EDGE,"E25.0"),sQuery(id+"F0.wireOp",EDGE,"E25.1"),sQuery(id+"F0.wireOp",EDGE,"E25.2"),sQuery(id+"F0.wireOp",EDGE,"E25.3"),sQuery(id+"F0.wireOp",EDGE,"E25.4"),sQuery(id+"F0.wireOp",EDGE,"E25.5"),sQuery(id+"F0.wireOp",EDGE,"E25.6"),sQuery(id+"F0.wireOp",EDGE,"E25.7")])],"isStart":false});
            extrude(context, id + "F17", {"entities" : qUnion([Q0, Q1, Q2]), "endBound" : BoundingType.UP_TO_SURFACE, "depth" : 25 * mm, "endBoundEntityFace" : qUnion([Q3]), "offsetDistance" : 25 * mm});
        }
    });
